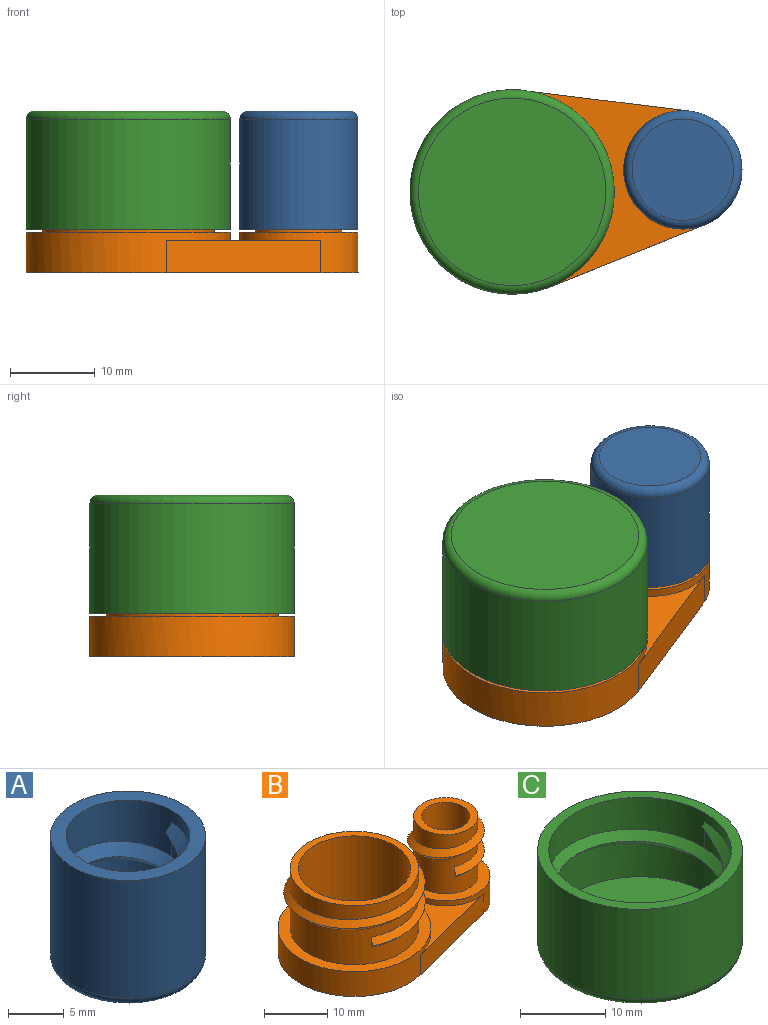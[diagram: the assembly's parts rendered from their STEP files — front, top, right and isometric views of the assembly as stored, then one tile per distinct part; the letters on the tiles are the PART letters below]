
ASSEMBLY  parts=3 mates=3
PART A: 12 faces, bbox 15.2x15.2x14 mm
  f0: cylinder r=6.99mm len=13.97mm, axis (0,0,-1), area 569.2mm2, adj f2,f3
  f1: plane 11.97x11.97mm, normal (0,0,-1), area 112.5mm2, adj f2
  f2: torus R=5.98mm, axis (0,0,1), area 65.4mm2, adj f0,f1
  f3: plane 13.97x13.97mm, normal (0,0,1), area 55.5mm2, adj f0,f11
  f4: plane 1.39x0.81mm, normal (0,1,0), area 0.5mm2, adj f5,f8,f11
  f5: bspline ~3.23x2.71mm, area 4.3mm2, adj f4,f6,f8,f10,f11
  f6: bspline ~12.89x11.16mm, area 55.6mm2, adj f5,f7,f8,f10
  f7: plane 2x0.87mm, normal (-0.87,0.5,0), area 1mm2, adj f6,f8,f10
  f8: bspline ~12.89x11.16mm, area 59.9mm2, adj f4,f5,f6,f7,f10,f11
  f9: plane 11.16x11.16mm, normal (0,0,1), area 97.8mm2, adj f10
  f10: cylinder r=5.58mm len=11.16mm, axis (0,0,-1), area 197mm2, adj f5,f6,f7,f8,f9,f11
  f11: cylinder r=5.58mm len=11.16mm, axis (0,0,-1), area 148.6mm2, adj f3,f4,f5,f8,f10
PART B: 26 faces, bbox 39.4x25.8x16.2 mm
  f0: plane 24.13x24.13mm, normal (0,0,1), area 133mm2, adj f1,f6
  f1: cylinder r=10.16mm len=20.32mm, axis (0,0,1), area 356.7mm2, adj f0,f2,f13,f14,f15
  f2: cylinder r=10.16mm len=20.32mm, axis (0,0,1), area 202.7mm2, adj f1,f12,f14,f20
  f3: plane 23.36x19.13mm, normal (0,0,1), area 94mm2, adj f4,f6,f7,f8
  f4: plane 19.03x5mm, normal (0.25,0.97,0), area 75mm2, adj f3,f5,f6,f8
  f5: plane 39.37x24.13mm, normal (0,0,-1), area 704.5mm2, adj f4,f6,f7,f8
  f6: cylinder r=12.06mm len=24.13mm, axis (0,0,-1), area 243.4mm2, adj f0,f3,f4,f5,f7
  f7: plane 19.07x4.84mm, normal (0.25,-0.97,0), area 75mm2, adj f3,f5,f6,f8
  f8: cylinder r=6.99mm len=13.97mm, axis (0,0,-1), area 114mm2, adj f3,f4,f5,f7,f11
  f9: cylinder r=5.08mm len=10.16mm, axis (0,0,1), area 178.4mm2, adj f10,f11,f17,f18,f19
  f10: cylinder r=5.08mm len=10.16mm, axis (0,0,1), area 101.3mm2, adj f9,f16,f18,f23
  f11: plane 13.97x13.97mm, normal (0,0,1), area 72.2mm2, adj f8,f9
  f12: plane 2x1mm, normal (0,1,0), area 1mm2, adj f2,f14,f15
  f13: plane 2x0.87mm, normal (-0.87,0.5,0), area 1mm2, adj f1,f14,f15
  f14: bspline ~25.77x22.32mm, area 126.4mm2, adj f1,f2,f12,f13,f15
  f15: bspline ~25.77x22.32mm, area 126.3mm2, adj f1,f12,f13,f14
  f16: plane 2x1mm, normal (0,1,0), area 1mm2, adj f10,f18,f19
  f17: plane 2x0.87mm, normal (-0.87,0.5,0), area 1mm2, adj f9,f18,f19
  f18: bspline ~14.04x12.16mm, area 66.3mm2, adj f9,f10,f16,f17,f19
  f19: bspline ~14.04x12.16mm, area 66.3mm2, adj f9,f16,f17,f18
  f20: plane 20.32x20.32mm, normal (0,0,1), area 76mm2, adj f2,f22
  f21: plane 17.78x17.78mm, normal (0,0,1), area 248.3mm2, adj f22
  f22: cylinder r=8.89mm len=17.78mm, axis (0,0,-1), area 836.2mm2, adj f20,f21
  f23: plane 10.16x10.16mm, normal (0,0,1), area 35.5mm2, adj f10,f25
  f24: plane 7.62x7.62mm, normal (0,0,1), area 45.6mm2, adj f25
  f25: cylinder r=3.81mm len=14.97mm, axis (0,0,-1), area 358.4mm2, adj f23,f24
PART C: 12 faces, bbox 26.1x26.1x14 mm
  f0: cylinder r=12.06mm len=24.13mm, axis (0,0,-1), area 983.2mm2, adj f2,f3
  f1: plane 22.13x22.13mm, normal (0,0,-1), area 384.6mm2, adj f2
  f2: torus R=11.06mm, axis (0,0,1), area 115.5mm2, adj f0,f1
  f3: plane 24.13x24.13mm, normal (0,0,1), area 94.3mm2, adj f0,f11
  f4: plane 0.86x0.45mm, normal (0,1,0), area 0.2mm2, adj f5,f8,f11
  f5: bspline ~3.49x2.35mm, area 3.8mm2, adj f4,f6,f8,f10
  f6: bspline ~24.83x21.5mm, area 116.5mm2, adj f5,f7,f8,f10
  f7: plane 2x0.87mm, normal (-0.87,0.5,0), area 1mm2, adj f6,f8,f10
  f8: bspline ~24.83x21.5mm, area 120.1mm2, adj f4,f5,f6,f7,f10,f11
  f9: plane 21.5x21.5mm, normal (0,0,1), area 363.1mm2, adj f10
  f10: cylinder r=10.75mm len=21.5mm, axis (0,0,-1), area 379.6mm2, adj f5,f6,f7,f8,f9,f11
  f11: cylinder r=10.75mm len=21.5mm, axis (0,0,-1), area 214.5mm2, adj f3,f4,f8,f10
PLACE A rot(axis=(1,0.07,0),180deg) t=(18.03,3.79,19.46)mm
PLACE B rot(axis=(0,0,1),7.6deg) t=(-2.12,1.18,0.38)mm fixed
PLACE C rot(axis=(1,0.07,0),180deg) t=(-2.12,1.18,19.46)mm
MATE slider A.f10 <-> B.f8  axis (0,0,-1) through (18.03,3.79,16.92)mm
MATE slider B.f22 <-> C.f10  axis (0,0,-1) through (-2.12,1.18,16.62)mm
MATE planar A.f0 <-> C.f0  axis (0,0,1) through (18.03,3.79,19.46)mm
